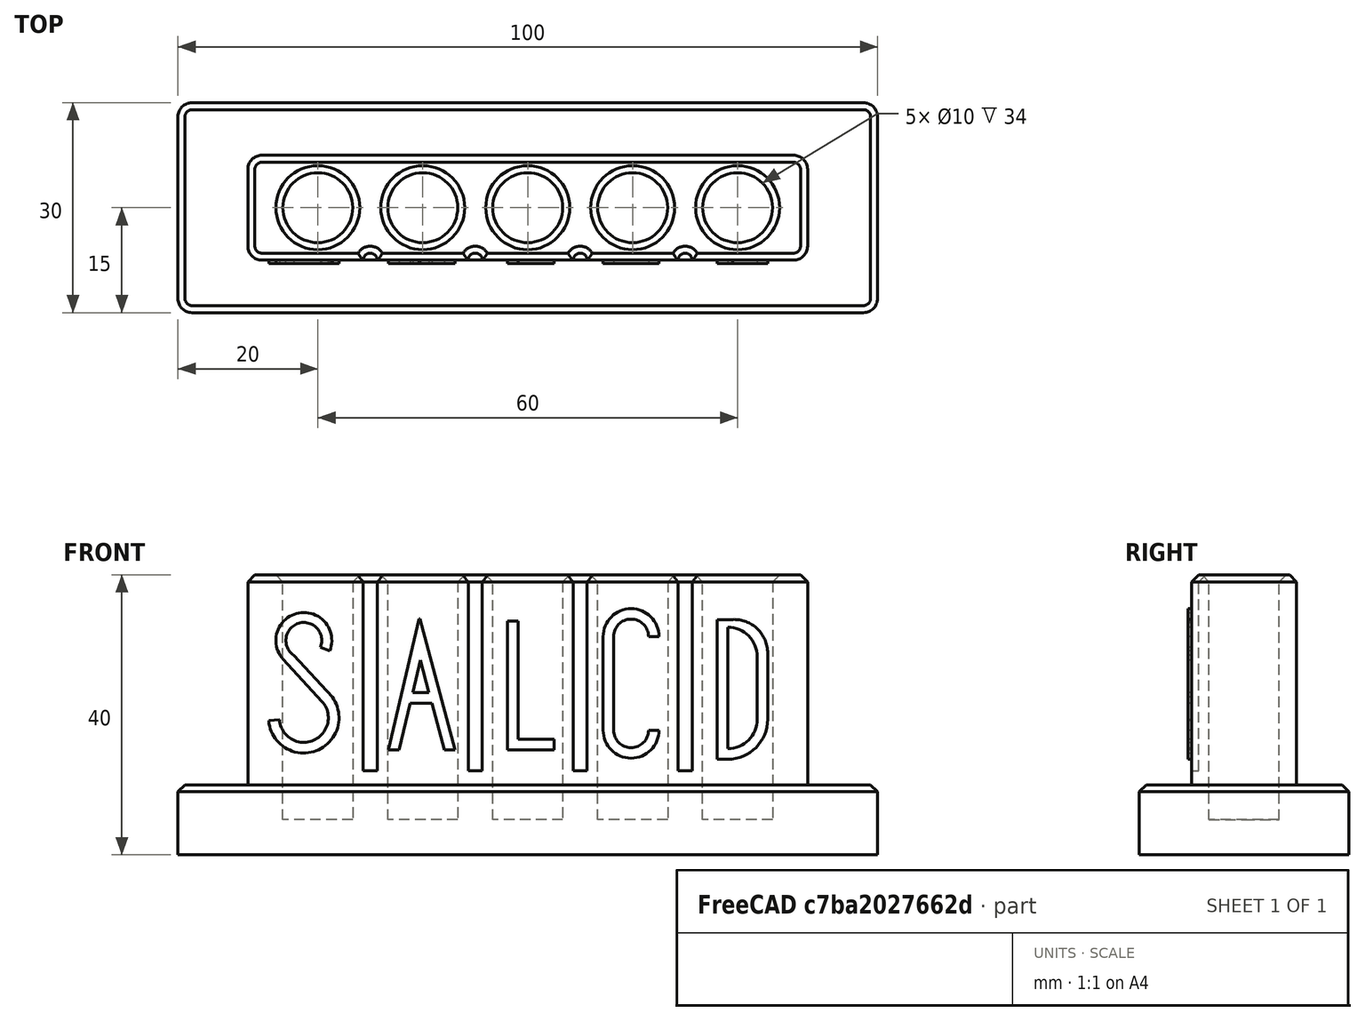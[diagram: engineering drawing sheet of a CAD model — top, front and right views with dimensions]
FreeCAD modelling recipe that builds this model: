
FCSTD DOCUMENT  (FreeCAD 0.19R)
Label: toothbrushholder
License: All rights reserved
LicenseURL: http://en.wikipedia.org/wiki/All_rights_reserved
objects: Sketcher::SketchObject×9, PartDesign::Pad×7, PartDesign::Pocket×2, PartDesign::Chamfer×2, PartDesign::LinearPattern×1, PartDesign::Fillet×1, PartDesign::Body×1, Mesh::Feature×1
note: 35 computed .brp shape members not serialized (recipe doc carries the construction recipe); baked Part::Feature solids carry a one-line shape summary decoded from their .brp

FEATURE [Sketcher::SketchObject] Sketch
  FullyConstrained = true
  MapMode = 5
  Support = -> [XY_Plane]
  sketch-geometry (4):
    g0: LineSegment StartX=-50 StartY=15 StartZ=0 EndX=50 EndY=15 EndZ=0
    g1: LineSegment StartX=50 StartY=15 StartZ=0 EndX=50 EndY=-15 EndZ=0
    g2: LineSegment StartX=50 StartY=-15 StartZ=0 EndX=-50 EndY=-15 EndZ=0
    g3: LineSegment StartX=-50 StartY=-15 StartZ=0 EndX=-50 EndY=15 EndZ=0
  constraints (11):
    c: Coincident(g0,g1)
    c: Coincident(g1,g2)
    c: Coincident(g2,g3)
    c: Coincident(g3,g0)
    c: Horizontal(g0)
    c: Horizontal(g2)
    c: Vertical(g1)
    c: Vertical(g3)
    c: Symmetric(g1,g0,g-1)
    c: Distance(g3) = 30
    c: Distance(g0) = 100
FEATURE [PartDesign::Pad] Pad
  Direction = (1,1,1)
  Length = 10
  Length2 = 100
  Profile = -> Sketch
  Type = 0
FEATURE [Sketcher::SketchObject] Sketch001
  FullyConstrained = true
  MapMode = 5
  Placement = pos=(0,0,10) rot=(0,0,1;0rad)
  Support = -> [Pad]
  sketch-geometry (4):
    g0: LineSegment StartX=-40 StartY=7.5 StartZ=0 EndX=40 EndY=7.5 EndZ=0
    g1: LineSegment StartX=40 StartY=7.5 StartZ=0 EndX=40 EndY=-7.5 EndZ=0
    g2: LineSegment StartX=40 StartY=-7.5 StartZ=0 EndX=-40 EndY=-7.5 EndZ=0
    g3: LineSegment StartX=-40 StartY=-7.5 StartZ=0 EndX=-40 EndY=7.5 EndZ=0
  constraints (11):
    c: Coincident(g0,g1)
    c: Coincident(g1,g2)
    c: Coincident(g2,g3)
    c: Coincident(g3,g0)
    c: Horizontal(g0)
    c: Horizontal(g2)
    c: Vertical(g1)
    c: Vertical(g3)
    c: Symmetric(g1,g0,g-1)
    c: Distance(g1) = 15
    c: Distance(g0) = 80
FEATURE [PartDesign::Pad] Pad001
  BaseFeature = -> Pad
  Direction = (1,1,1)
  Length = 30
  Length2 = 100
  Profile = -> Sketch001
  Type = 0
FEATURE [Sketcher::SketchObject] Sketch002
  FullyConstrained = true
  MapMode = 5
  Placement = pos=(0,0,40) rot=(0,0,1;0rad)
  Support = -> [Pad001]
  sketch-geometry (1):
    g0: Circle CenterX=-30 CenterY=0 CenterZ=0 NormalX=0 NormalY=0 NormalZ=1 AngleXU=0 Radius=5
  constraints (3):
    c: Radius(g0) = 5
    c: PointOnObject(g0,g-1)
    c: DistanceX(g0) = -30
FEATURE [PartDesign::Pocket] Pocket
  BaseFeature = -> Pad001
  Length = 35
  Length2 = 100
  Profile = -> Sketch002
  Type = 0
FEATURE [PartDesign::LinearPattern] LinearPattern
  BaseFeature = -> Pocket
  Direction = -> X_Axis
  Length = 60
  Occurrences = 5
  Originals = -> [Pocket]
FEATURE [Sketcher::SketchObject] Sketch004
  ExternalGeometry = -> [LinearPattern]
  FullyConstrained = true
  MapMode = 5
  Placement = pos=(0,0,40) rot=(0,0,1;0rad)
  Support = -> [LinearPattern]
  sketch-geometry (4):
    g0: Circle CenterX=-22.5 CenterY=-7.5 CenterZ=0 NormalX=0 NormalY=0 NormalZ=1 AngleXU=0 Radius=1
    g1: Circle CenterX=-7.5 CenterY=-7.5 CenterZ=0 NormalX=0 NormalY=0 NormalZ=1 AngleXU=0 Radius=1
    g2: Circle CenterX=7.5 CenterY=-7.5 CenterZ=0 NormalX=0 NormalY=0 NormalZ=1 AngleXU=0 Radius=1
    g3: Circle CenterX=22.5 CenterY=-7.5 CenterZ=0 NormalX=0 NormalY=0 NormalZ=1 AngleXU=0 Radius=1
  constraints (12):
    c: Radius(g0) = 1
    c: Equal(g0,g1)
    c: Equal(g0,g2)
    c: Equal(g0,g3)
    c: PointOnObject(g0,g-3)
    c: PointOnObject(g1,g-3)
    c: PointOnObject(g3,g-3)
    c: PointOnObject(g2,g-3)
    c: DistanceX(g2) = 7.5
    c: DistanceX(g3) = 22.5
    c: DistanceX(g1) = -7.5
    c: DistanceX(g0) = -22.5
FEATURE [PartDesign::Pocket] Pocket001
  BaseFeature = -> LinearPattern
  Length = 28
  Length2 = 100
  Profile = -> Sketch004
  Type = 0
FEATURE [Sketcher::SketchObject] Sketch005
  FullyConstrained = false
  MapMode = 5
  Placement = pos=(0,-7.5,0) rot=(1,0,0;1.5708rad)
  Support = -> [Pocket001]
  sketch-geometry (8):
    g0: ArcOfCircle CenterX=-32 CenterY=30.6258 CenterZ=0 NormalX=0 NormalY=0 NormalZ=1 AngleXU=0 Radius=4 StartAngle=5.90042 EndAngle=10.1696
    g1: ArcOfCircle CenterX=-32 CenterY=19.5612 CenterZ=0 NormalX=0 NormalY=0 NormalZ=1 AngleXU=0 Radius=3.5 StartAngle=3.22424 EndAngle=7.02801
    g2: LineSegment StartX=-34.9408 StartY=27.9144 StartZ=0 EndX=-29.4268 EndY=21.9336 EndZ=0
    g3: LineSegment StartX=-28.2895 StartY=29.1318 StartZ=0 EndX=-29.6177 EndY=29.6666 EndZ=0
    g4: LineSegment StartX=-33.4398 StartY=28.4992 StartZ=0 EndX=-27.9455 EndY=22.5399 EndZ=0
    g5: LineSegment StartX=-35.4881 StartY=19.2723 StartZ=0 EndX=-37.0139 EndY=19.1459 EndZ=0
    g6: ArcOfCircle CenterX=-32 CenterY=19.5612 CenterZ=0 NormalX=0 NormalY=0 NormalZ=1 AngleXU=0 Radius=5.03108 StartAngle=3.22424 EndAngle=6.9168
    g7: ArcOfCircle CenterX=-32 CenterY=30.6258 CenterZ=0 NormalX=0 NormalY=0 NormalZ=1 AngleXU=0 Radius=2.5681 StartAngle=5.90042 EndAngle=10.4004
  constraints (18):
    c: Tangent(g2,g1) = 1.5708
    c: Tangent(g2,g0) = -1.5708
    c: Radius(g1) = 3.5
    c: Radius(g0) = 4
    c: Coincident(g3,g0)
    c: Coincident(g5,g1)
    c: Coincident(g6,g1)
    c: Coincident(g6,g5)
    c: Coincident(g7,g0)
    c: Coincident(g7,g3)
    c: Coincident(g4,g7)
    c: Coincident(g6,g4)
    c: Parallel(g4,g2)
    c: Perpendicular(g6,g5)
    c: Perpendicular(g0,g3)
    c: Distance(g1,g4) = 1.5
    c: DistanceX(g1) = -32
    c: DistanceX(g0) = -32
FEATURE [PartDesign::Pad] Pad002
  BaseFeature = -> Pocket001
  Direction = (1,1,1)
  Length = 0.5
  Length2 = 100
  Profile = -> Sketch005
  Type = 0
FEATURE [Sketcher::SketchObject] Sketch006
  FullyConstrained = false
  MapMode = 5
  Placement = pos=(0,-7.5,0) rot=(1,0,0;1.5708rad)
  Support = -> [Pad002]
  sketch-geometry (11):
    g0: LineSegment StartX=-15.5082 StartY=33.687 StartZ=0 EndX=-19.8897 EndY=15 EndZ=0
    g1: LineSegment StartX=-19.8897 StartY=15 StartZ=0 EndX=-18.3897 EndY=15 EndZ=0
    g2: LineSegment StartX=-18.3897 StartY=15 StartZ=0 EndX=-16.8235 EndY=21.6798 EndZ=0
    g3: LineSegment StartX=-16.8235 StartY=21.6798 StartZ=0 EndX=-13.6709 EndY=21.6798 EndZ=0
    g4: LineSegment StartX=-13.6709 StartY=21.6798 StartZ=0 EndX=-11.8894 EndY=15 EndZ=0
    g5: LineSegment StartX=-11.8894 StartY=15 StartZ=0 EndX=-10.3894 EndY=15 EndZ=0
    g6: LineSegment StartX=-10.3894 StartY=15 StartZ=0 EndX=-15.3731 EndY=33.687 EndZ=0
    g7: LineSegment StartX=-15.3731 StartY=33.687 StartZ=0 EndX=-15.5082 EndY=33.687 EndZ=0
    g8: LineSegment StartX=-15.3514 StartY=27.7847 StartZ=0 EndX=-16.4311 EndY=23.1798 EndZ=0
    g9: LineSegment StartX=-16.4311 StartY=23.1798 StartZ=0 EndX=-14.1233 EndY=23.1798 EndZ=0
    g10: LineSegment StartX=-14.1233 StartY=23.1798 StartZ=0 EndX=-15.3514 EndY=27.7847 EndZ=0
  constraints (27):
    c: Coincident(g0,g1)
    c: Coincident(g1,g2)
    c: Coincident(g2,g3)
    c: Coincident(g3,g4)
    c: Coincident(g4,g5)
    c: Coincident(g5,g6)
    c: Coincident(g6,g7)
    c: Coincident(g7,g0)
    c: Coincident(g8,g9)
    c: Coincident(g9,g10)
    c: Coincident(g10,g8)
    c: Horizontal(g5)
    c: Horizontal(g1)
    c: Horizontal(g3)
    c: Horizontal(g9)
    c: Horizontal(g7)
    c: Distance(g1) = 1.5
    c: Distance(g5) = 1.5
    c: Parallel(g2,g0)
    c: Parallel(g4,g6)
    c: Parallel(g10,g6)
    c: Parallel(g0,g8)
    c: DistanceY(g1) = 15
    c: DistanceY(g5) = 15
    c: Distance(g9,g3) = 1.5
    c: Distance(g8,g0) = 1.5
    c: Distance(g9,g6) = 1.5
FEATURE [PartDesign::Pad] Pad003
  BaseFeature = -> Pad002
  Direction = (1,1,1)
  Length = 0.5
  Length2 = 100
  Profile = -> Sketch006
  Type = 0
FEATURE [Sketcher::SketchObject] Sketch007
  FullyConstrained = false
  MapMode = 5
  Placement = pos=(0,-7.5,0) rot=(1,0,0;1.5708rad)
  Support = -> [Pad003]
  sketch-geometry (6):
    g0: LineSegment StartX=-2.89718 StartY=33.4173 StartZ=0 EndX=-2.89718 EndY=15 EndZ=0
    g1: LineSegment StartX=-2.89718 StartY=15 StartZ=0 EndX=3.77357 EndY=15 EndZ=0
    g2: LineSegment StartX=3.77357 StartY=15 StartZ=0 EndX=3.77357 EndY=16.5 EndZ=0
    g3: LineSegment StartX=3.77357 StartY=16.5 StartZ=0 EndX=-1.39718 EndY=16.5 EndZ=0
    g4: LineSegment StartX=-1.39718 StartY=16.5 StartZ=0 EndX=-1.39718 EndY=33.4173 EndZ=0
    g5: LineSegment StartX=-1.39718 StartY=33.4173 StartZ=0 EndX=-2.89718 EndY=33.4173 EndZ=0
  constraints (15):
    c: Vertical(g0)
    c: Coincident(g0,g1)
    c: Horizontal(g1)
    c: Coincident(g1,g2)
    c: Coincident(g2,g3)
    c: Horizontal(g3)
    c: Coincident(g3,g4)
    c: Vertical(g4)
    c: Coincident(g4,g5)
    c: Coincident(g5,g0)
    c: Horizontal(g5)
    c: Vertical(g2)
    c: Distance(g2) = 1.5
    c: Distance(g5) = 1.5
    c: DistanceY(g0) = 15
FEATURE [PartDesign::Pad] Pad004
  BaseFeature = -> Pad003
  Direction = (1,1,1)
  Length = 0.5
  Length2 = 100
  Profile = -> Sketch007
  Type = 0
FEATURE [Sketcher::SketchObject] Sketch008
  FullyConstrained = false
  MapMode = 5
  Placement = pos=(0,-7.5,0) rot=(1,0,0;1.5708rad)
  Support = -> [Pad004]
  sketch-geometry (8):
    g0: ArcOfCircle CenterX=14.7727 CenterY=31.1737 CenterZ=0 NormalX=0 NormalY=0 NormalZ=1 AngleXU=0 Radius=4 StartAngle=-1.15e-14 EndAngle=3.14159
    g1: ArcOfCircle CenterX=14.7727 CenterY=17.8087 CenterZ=0 NormalX=0 NormalY=0 NormalZ=1 AngleXU=0 Radius=4 StartAngle=3.14159 EndAngle=6.28319
    g2: ArcOfCircle CenterX=14.7727 CenterY=31.1737 CenterZ=0 NormalX=0 NormalY=0 NormalZ=1 AngleXU=0 Radius=2.5 StartAngle=-1.78e-14 EndAngle=3.14159
    g3: ArcOfCircle CenterX=14.7727 CenterY=17.8087 CenterZ=0 NormalX=0 NormalY=0 NormalZ=1 AngleXU=0 Radius=2.5 StartAngle=3.14159 EndAngle=6.28319
    g4: LineSegment StartX=10.7727 StartY=17.8087 StartZ=0 EndX=10.7727 EndY=31.1737 EndZ=0
    g5: LineSegment StartX=12.2727 StartY=31.1737 StartZ=0 EndX=12.2727 EndY=17.8087 EndZ=0
    g6: LineSegment StartX=17.2727 StartY=17.8087 StartZ=0 EndX=18.7727 EndY=17.8087 EndZ=0
    g7: LineSegment StartX=17.2727 StartY=31.1737 StartZ=0 EndX=18.7727 EndY=31.1737 EndZ=0
  constraints (19):
    c: Coincident(g2,g0)
    c: Coincident(g3,g1)
    c: Vertical(g5)
    c: Coincident(g6,g3)
    c: Coincident(g6,g1)
    c: Coincident(g7,g2)
    c: Coincident(g7,g0)
    c: Horizontal(g7)
    c: Horizontal(g6)
    c: Perpendicular(g2,g7)
    c: Perpendicular(g3,g6)
    c: Vertical(g4)
    c: Tangent(g4,g0) = 1.5708
    c: Tangent(g4,g1) = 1.5708
    c: Radius(g2) = 2.5
    c: Distance(g2,g4) = 1.5
    c: Tangent(g5,g3) = -1.5708
    c: Radius(g3) = 2.5
    c: Tangent(g5,g2) = -1.5708
FEATURE [PartDesign::Pad] Pad005
  BaseFeature = -> Pad004
  Direction = (1,1,1)
  Length = 0.5
  Length2 = 100
  Profile = -> Sketch008
  Type = 0
FEATURE [Sketcher::SketchObject] Sketch009
  FullyConstrained = false
  MapMode = 5
  Placement = pos=(0,-7.5,0) rot=(1,0,0;1.5708rad)
  Support = -> [Pad005]
  sketch-geometry (10):
    g0: ArcOfCircle CenterX=28.5981 CenterY=19.3607 CenterZ=0 NormalX=0 NormalY=0 NormalZ=1 AngleXU=0 Radius=4.21068 StartAngle=4.71239 EndAngle=6.28319
    g1: LineSegment StartX=28.5981 StartY=32.5056 StartZ=0 EndX=28.5981 EndY=15.15 EndZ=0
    g2: LineSegment StartX=32.8088 StartY=19.3607 StartZ=0 EndX=32.8088 EndY=28.2949 EndZ=0
    g3: LineSegment StartX=27.0981 StartY=33.6204 StartZ=0 EndX=27.0981 EndY=13.65 EndZ=0
    g4: ArcOfCircle CenterX=28.5981 CenterY=19.3607 CenterZ=0 NormalX=0 NormalY=0 NormalZ=1 AngleXU=0 Radius=5.71068 StartAngle=4.71239 EndAngle=6.28319
    g5: LineSegment StartX=34.3088 StartY=28.8139 StartZ=0 EndX=34.3088 EndY=19.3607 EndZ=0
    g6: LineSegment StartX=27.0981 StartY=13.65 StartZ=0 EndX=28.5981 EndY=13.65 EndZ=0
    g7: LineSegment StartX=27.0981 StartY=33.6204 StartZ=0 EndX=29.2832 EndY=33.6204 EndZ=0
    g8: ArcOfCircle CenterX=28.5981 CenterY=28.2949 CenterZ=0 NormalX=0 NormalY=0 NormalZ=1 AngleXU=0 Radius=4.21068 StartAngle=0 EndAngle=1.5708
    g9: ArcOfCircle CenterX=29.4975 CenterY=28.8139 CenterZ=0 NormalX=0 NormalY=0 NormalZ=1 AngleXU=0 Radius=4.81128 StartAngle=2e-16 EndAngle=1.61535
  constraints (21):
    c: Vertical(g2)
    c: Tangent(g2,g0) = -1.5708
    c: Vertical(g5)
    c: Tangent(g5,g4) = 1.5708
    c: Coincident(g6,g3)
    c: Perpendicular(g3,g6)
    c: Coincident(g7,g3)
    c: Perpendicular(g3,g7)
    c: Coincident(g0,g1)
    c: Tangent(g6,g4) = -1.5708
    c: Vertical(g3)
    c: Coincident(g0,g4)
    c: Parallel(g1,g3)
    c: Perpendicular(g0,g1)
    c: Coincident(g8,g1)
    c: Perpendicular(g8,g1)
    c: Tangent(g8,g2) = -1.5708
    c: Distance(g0,g3) = 1.5
    c: Distance(g0,g5) = 1.5
    c: Tangent(g9,g5) = 1.5708
    c: Coincident(g9,g7)
FEATURE [PartDesign::Pad] Pad006
  BaseFeature = -> Pad005
  Direction = (1,1,1)
  Length = 0.5
  Length2 = 100
  Profile = -> Sketch009
  Type = 0
FEATURE [PartDesign::Fillet] Fillet
  Base = -> Pad006 [Edge20,Edge18,Edge2,Edge8,Edge22,Edge5,Edge17,Edge1]
  BaseFeature = -> Pad006
  Radius = 2
  SupportTransform = false
FEATURE [PartDesign::Chamfer] Chamfer
  Angle = 45
  Base = -> Fillet [Edge20]
  BaseFeature = -> Fillet
  ChamferType = 0
  FlipDirection = false
  Size = 1
  Size2 = 1
  SupportTransform = false
FEATURE [PartDesign::Chamfer] Chamfer001
  Angle = 45
  Base = -> Chamfer [Face27]
  BaseFeature = -> Chamfer
  ChamferType = 0
  FlipDirection = false
  Size = 1
  Size2 = 1
  SupportTransform = false
FEATURE [PartDesign::Body] Body
  Group = -> [Sketch,Pad,Sketch001,Pad001,Sketch002,Pocket,LinearPattern,Sketch004,Pocket001,Sketch005,Pad002,Sketch006,Pad003,Sketch007,Pad004,Sketch008,Pad005,Sketch009,Pad006,Fillet,Chamfer,Chamfer001]
  Origin = -> Origin
  Tip = -> Chamfer001
FEATURE [Mesh::Feature] Mesh  label="Chamfer001 (Meshed)"
